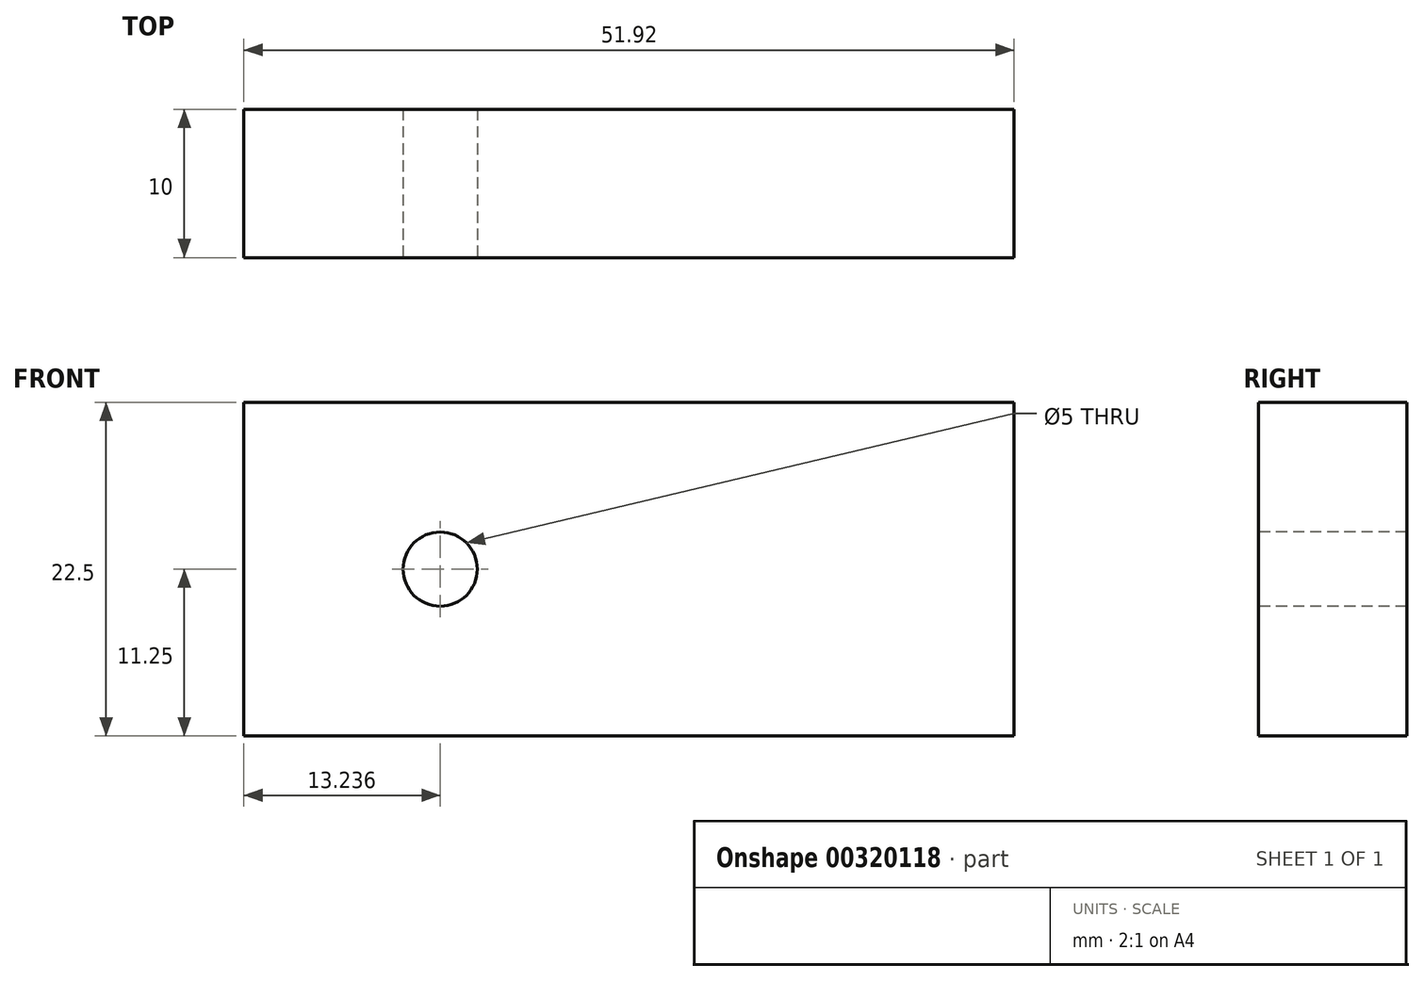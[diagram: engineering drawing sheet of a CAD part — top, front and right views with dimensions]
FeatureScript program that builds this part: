
annotation { "Feature Type Name" : "Feature", "Feature Type Description" : "" }
export const myFeature = defineFeature(function(context is Context, id is Id, definition is map)
    precondition{}
    {
        {
            var Q0;
            Q0=qCreatedBy(makeId("Front.planeOp"),FACE);
            var sketch = newSketch(context, id + "F0", { "sketchPlane" : qUnion([Q0])});
            skLineSegment(sketch, "E0.bottom", {"start": v(25.96, 11.25) * mm, "end": v(-25.96, 11.25) * mm});
            skLineSegment(sketch, "E0.top", {"start": v(25.96, -11.25) * mm, "end": v(-25.96, -11.25) * mm});
            skLineSegment(sketch, "E0.left", {"start": v(25.96, 11.25) * mm, "end": v(25.96, -11.25) * mm});
            skLineSegment(sketch, "E0.right", {"start": v(-25.96, 11.25) * mm, "end": v(-25.96, -11.25) * mm});
            skPoint(sketch, "E0.middle", {"position": v(0, 0) * mm});
            skSolve(sketch);
        }
        {
            var Q0;
            Q0=makeQuery(id+"F0.imprint","IMPRINT",FACE,{"disambiguationData":[TD([[makeQuery(id+"F0.imprint","IMPRINT",EDGE,{"derivedFrom":sQuery(id+"F0.wireOp",EDGE,"E0.bottom")}),1.0]])]});
            extrude(context, id + "F1", {"entities" : qUnion([Q0]), "depth" : 10 * mm});
        }
        {
            var Q0;
            Q0=makeQuery(id+"F1.opExtrude","CAP_FACE",FACE,{"disambiguationData":[OSD([sQuery(id+"F0.wireOp",EDGE,"E0.bottom"),sQuery(id+"F0.wireOp",EDGE,"E0.top"),sQuery(id+"F0.wireOp",EDGE,"E0.left"),sQuery(id+"F0.wireOp",EDGE,"E0.right")])],"isStart":false});
            var sketch = newSketch(context, id + "F2", { "sketchPlane" : qUnion([Q0])});
            skPoint(sketch, "E1", {"position": v(-12.72, 0) * mm});
            skSolve(sketch);
        }
        {
            var Q0;
            Q0=sQuery(id+"F2.wireOp",VERTEX,"E1");
            var Q1;
            Q1=makeQuery(id+"F1.opExtrude","SWEPT_BODY",BODY,{"disambiguationData":[OSD([sQuery(id+"F0.wireOp",EDGE,"E0.bottom"),sQuery(id+"F0.wireOp",EDGE,"E0.top"),sQuery(id+"F0.wireOp",EDGE,"E0.left"),sQuery(id+"F0.wireOp",EDGE,"E0.right")])]});
            hole(context, id + "F3", {"style" : HoleStyle.SIMPLE, "endStyle" : HoleEndStyle.THROUGH, "holeDiameter" : 5 * mm, "tappedDepth" : 12 * mm, "tapClearance" : 3, "locations" : qUnion([Q0]), "scope" : qUnion([Q1])});
        }
    });
